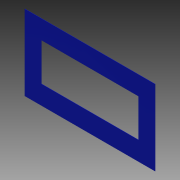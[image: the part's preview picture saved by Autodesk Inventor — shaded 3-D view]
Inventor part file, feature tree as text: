
AUTODESK INVENTOR PART (.ipt)
format: ipt  version: 2013 (Build 170138000, 138)  size: 83,968 bytes
history: native  units: in
note: dims shown in document units (in); Inventor stores cm internally (conversion verified against a paired STEP export)
features: extrude x2, sketch x2
ambient origin geometry x8: Origin, YZ Plane, XZ Plane, XY Plane, X Axis, Y Axis, Z Axis, Center Point
bodies: Solid1 (feature_tree)
feature tree (4):
  extrude  "Extrusion1"  Depth=42.0in
  extrude  "Extrusion2"  Depth=9.25in
  sketch  "Sketch1"  dims[d0=72.5in d1=42.0in]
  sketch  "Sketch2"  dims[d2=0.125in d3=0.0in d4=9.25in d5=10.5in d6=9.25in d7=10.5in d8=1.0in d9=0.0in]
